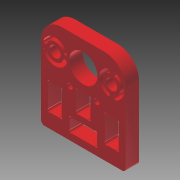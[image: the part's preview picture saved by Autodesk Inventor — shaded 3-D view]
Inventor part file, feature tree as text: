
AUTODESK INVENTOR PART (.ipt)
format: ipt  version: 2012 SP1 (Build 160190100, 190)  size: 244,736 bytes
history: native  units: in
note: dims shown in document units (in); Inventor stores cm internally (conversion verified against a paired STEP export)
features: other x5, extrude x2
ambient origin geometry x8: Origin, YZ Plane, XZ Plane, XY Plane, X Axis, Y Axis, Z Axis, Center Point
bodies: Solid1 (feature_tree)
feature tree (7):
  other  "skeleton.ipt"
  other  "DRILL-THROUGH"
  other  "POCKET_3-8"
  other  "STOCK_12MM"
  extrude  "Extrusion1"  Depth=0.3937in
  extrude  "Extrusion2"  Depth=0.4724in
  other  "THROUGH-CUT"
